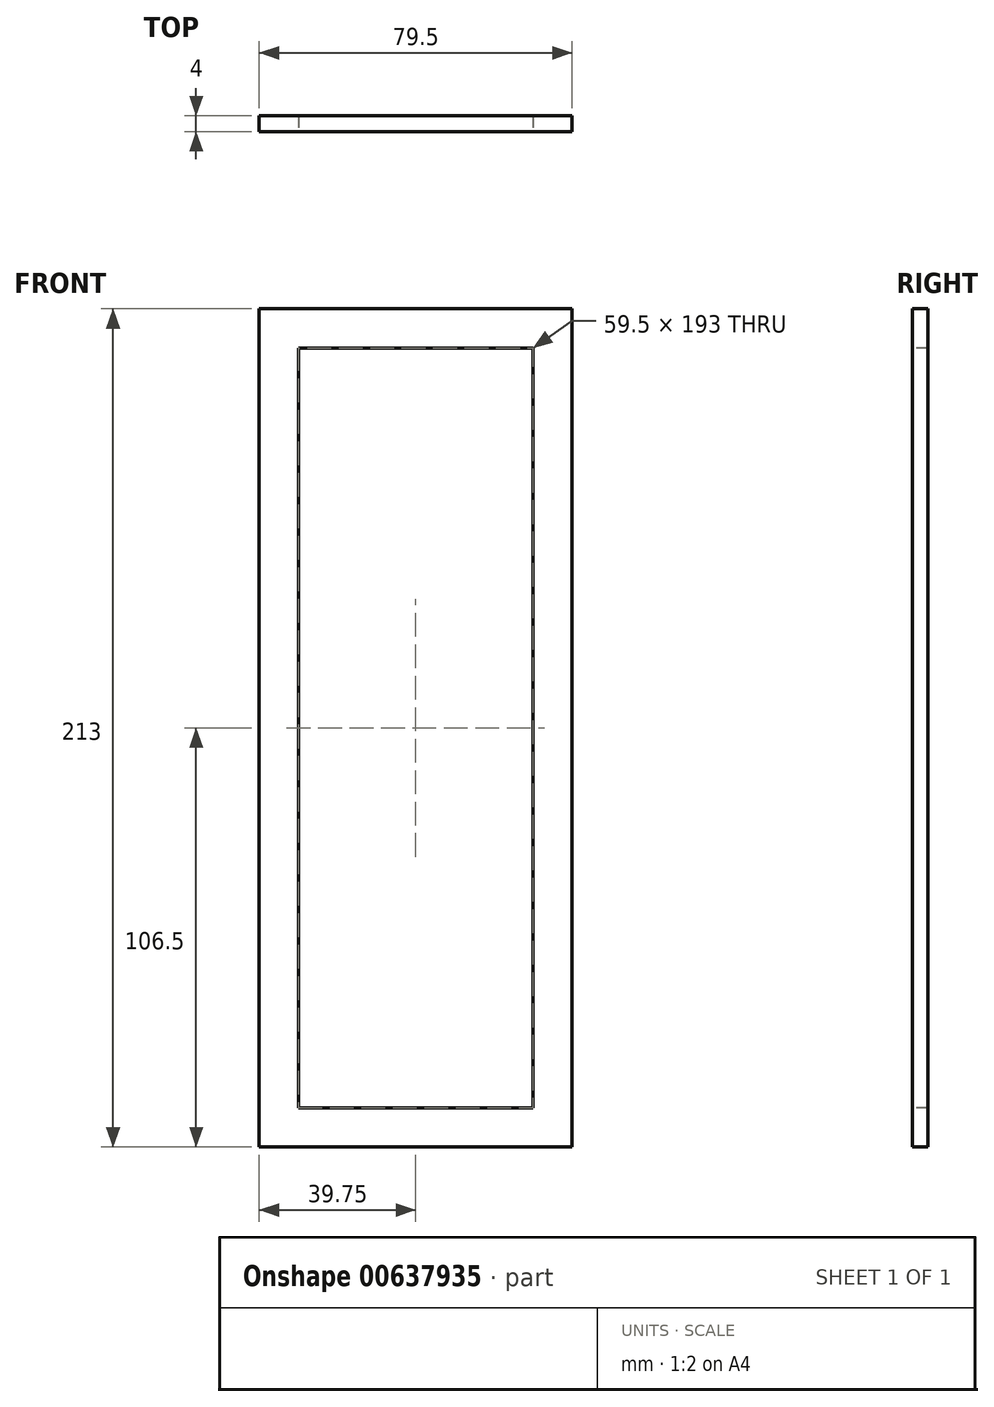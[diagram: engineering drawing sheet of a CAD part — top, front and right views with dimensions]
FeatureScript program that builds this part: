
annotation { "Feature Type Name" : "Feature", "Feature Type Description" : "" }
export const myFeature = defineFeature(function(context is Context, id is Id, definition is map)
    precondition{}
    {
        {
            var Q0;
            Q0=qCreatedBy(makeId("Front.planeOp"),FACE);
            var sketch = newSketch(context, id + "F0", { "sketchPlane" : qUnion([Q0])});
            skLineSegment(sketch, "E0", {"start": v(0, 0) * mm, "end": v(0, 213) * mm});
            skLineSegment(sketch, "E1", {"start": v(0, 213) * mm, "end": v(79.5, 213) * mm});
            skLineSegment(sketch, "E2", {"start": v(79.5, 213) * mm, "end": v(79.5, 0) * mm});
            skLineSegment(sketch, "E3", {"start": v(79.5, 0) * mm, "end": v(0, 0) * mm});
            skSolve(sketch);
        }
        {
            var Q0;
            Q0=makeQuery(id+"F0.imprint","IMPRINT",FACE,{"disambiguationData":[TD([[makeQuery(id+"F0.imprint","IMPRINT",EDGE,{"derivedFrom":sQuery(id+"F0.wireOp",EDGE,"E0")}),-1.0]])]});
            extrude(context, id + "F1", {"entities" : qUnion([Q0]), "depth" : 4 * mm, "offsetDistance" : 25 * mm});
        }
        {
            var Q0;
            Q0=makeQuery(id+"F1.opExtrude","CAP_FACE",FACE,{"disambiguationData":[OSD([sQuery(id+"F0.wireOp",EDGE,"E0"),sQuery(id+"F0.wireOp",EDGE,"E1"),sQuery(id+"F0.wireOp",EDGE,"E2"),sQuery(id+"F0.wireOp",EDGE,"E3")])],"isStart":false});
            var sketch = newSketch(context, id + "F2", { "sketchPlane" : qUnion([Q0])});
            skLineSegment(sketch, "E4.0", {"start": v(10, 10) * mm, "end": v(69.5, 10) * mm});
            skLineSegment(sketch, "E4.1", {"start": v(10, 203) * mm, "end": v(10, 10) * mm});
            skLineSegment(sketch, "E4.2", {"start": v(69.5, 203) * mm, "end": v(10, 203) * mm});
            skLineSegment(sketch, "E4.3", {"start": v(69.5, 10) * mm, "end": v(69.5, 203) * mm});
            skSolve(sketch);
        }
        {
            var Q0;
            Q0=makeQuery(id+"F2.imprint","IMPRINT",FACE,{"disambiguationData":[TD([[makeQuery(id+"F2.imprint","IMPRINT",EDGE,{"derivedFrom":sQuery(id+"F2.wireOp",EDGE,"E4.0")}),1.0]])]});
            extrude(context, id + "F3", {"entities" : qUnion([Q0]), "operationType" : NewBodyOperationType.REMOVE, "endBound" : BoundingType.UP_TO_NEXT, "oppositeDirection" : true, "depth" : 25 * mm, "offsetDistance" : 25 * mm});
        }
    });
